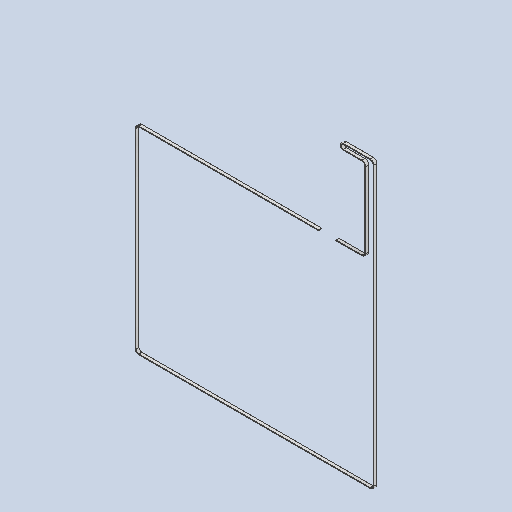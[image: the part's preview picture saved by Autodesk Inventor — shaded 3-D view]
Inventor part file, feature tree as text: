
AUTODESK INVENTOR PART (.ipt)
format: ipt  version: 2024.2 (Build 282272000, 272)  size: 105,984 bytes
history: native  units: in
note: dims shown in document units (in); Inventor stores cm internally (conversion verified against a paired STEP export)
features: sweep x1
ambient origin geometry x8: Origin, YZ Plane, XZ Plane, XY Plane, X Axis, Y Axis, Z Axis, Center Point
bodies: Solid1 (feature_tree)
feature tree (1):
  sweep  "Sweep1"
